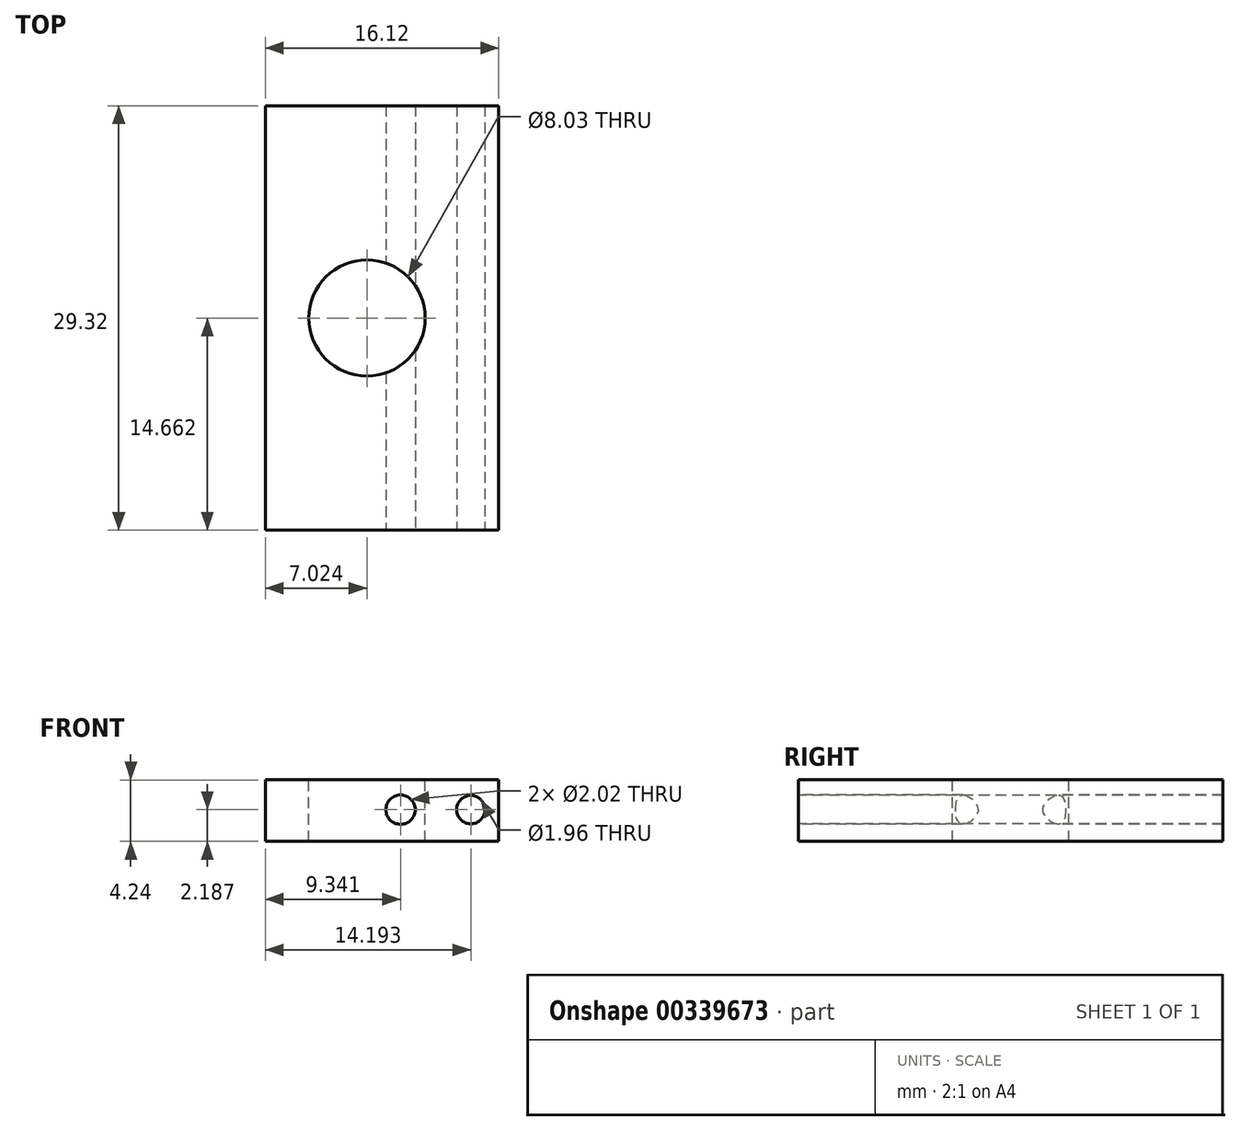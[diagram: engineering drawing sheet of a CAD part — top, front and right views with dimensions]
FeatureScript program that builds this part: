
annotation { "Feature Type Name" : "Feature", "Feature Type Description" : "" }
export const myFeature = defineFeature(function(context is Context, id is Id, definition is map)
    precondition{}
    {
        {
            var Q0;
            Q0=qCreatedBy(makeId("Front.planeOp"),FACE);
            var sketch = newSketch(context, id + "F0", { "sketchPlane" : qUnion([Q0])});
            skLineSegment(sketch, "E0.bottom", {"start": v(0, 0) * mm, "end": v(16.12, 0) * mm});
            skLineSegment(sketch, "E0.top", {"start": v(0, 4.24) * mm, "end": v(16.12, 4.24) * mm});
            skLineSegment(sketch, "E0.left", {"start": v(0, 0) * mm, "end": v(0, 4.24) * mm});
            skLineSegment(sketch, "E0.right", {"start": v(16.12, 0) * mm, "end": v(16.12, 4.24) * mm});
            skSolve(sketch);
        }
        {
            var Q0;
            Q0=makeQuery(id+"F0.imprint","IMPRINT",FACE,{"disambiguationData":[TD([[makeQuery(id+"F0.imprint","IMPRINT",EDGE,{"derivedFrom":sQuery(id+"F0.wireOp",EDGE,"E0.bottom")}),1.0]])]});
            var sketch = newSketch(context, id + "F1", { "sketchPlane" : qUnion([Q0])});
            skCircle(sketch, "E1", {"center": v(14.2, 2.19) * mm, "radius": 0.98 * mm});
            skCircle(sketch, "E2", {"center": v(9.34, 2.19) * mm, "radius": 1.01 * mm});
            skLineSegment(sketch, "E3", {"start": v(8.33, 2.13) * mm, "end": v(7.11, 2.13) * mm});
            skSolve(sketch);
        }
        {
            var Q0;
            Q0 = qSketchRegion(id + "F0", true);
            extrude(context, id + "F2", {"entities" : qUnion([Q0]), "oppositeDirection" : true, "depth" : 29.32 * mm});
        }
        {
            var Q0;
            Q0 = qSketchRegion(id + "F1", true);
            extrude(context, id + "F3", {"entities" : qUnion([Q0]), "operationType" : NewBodyOperationType.REMOVE, "oppositeDirection" : true, "depth" : 42.4 * mm});
        }
        {
            var Q0;
            Q0=makeQuery(id+"F2.opExtrude","SWEPT_FACE",FACE,{"disambiguationData":[OSD([sQuery(id+"F0.wireOp",EDGE,"E0.top")])]});
            var sketch = newSketch(context, id + "F4", { "sketchPlane" : qUnion([Q0])});
            skCircle(sketch, "E4", {"center": v(7.02, 14.66) * mm, "radius": 4.02 * mm});
            skSolve(sketch);
        }
        {
            var Q0;
            Q0 = qSketchRegion(id + "F4", true);
            extrude(context, id + "F5", {"entities" : qUnion([Q0]), "operationType" : NewBodyOperationType.REMOVE, "oppositeDirection" : true, "depth" : 25 * mm});
        }
    });
